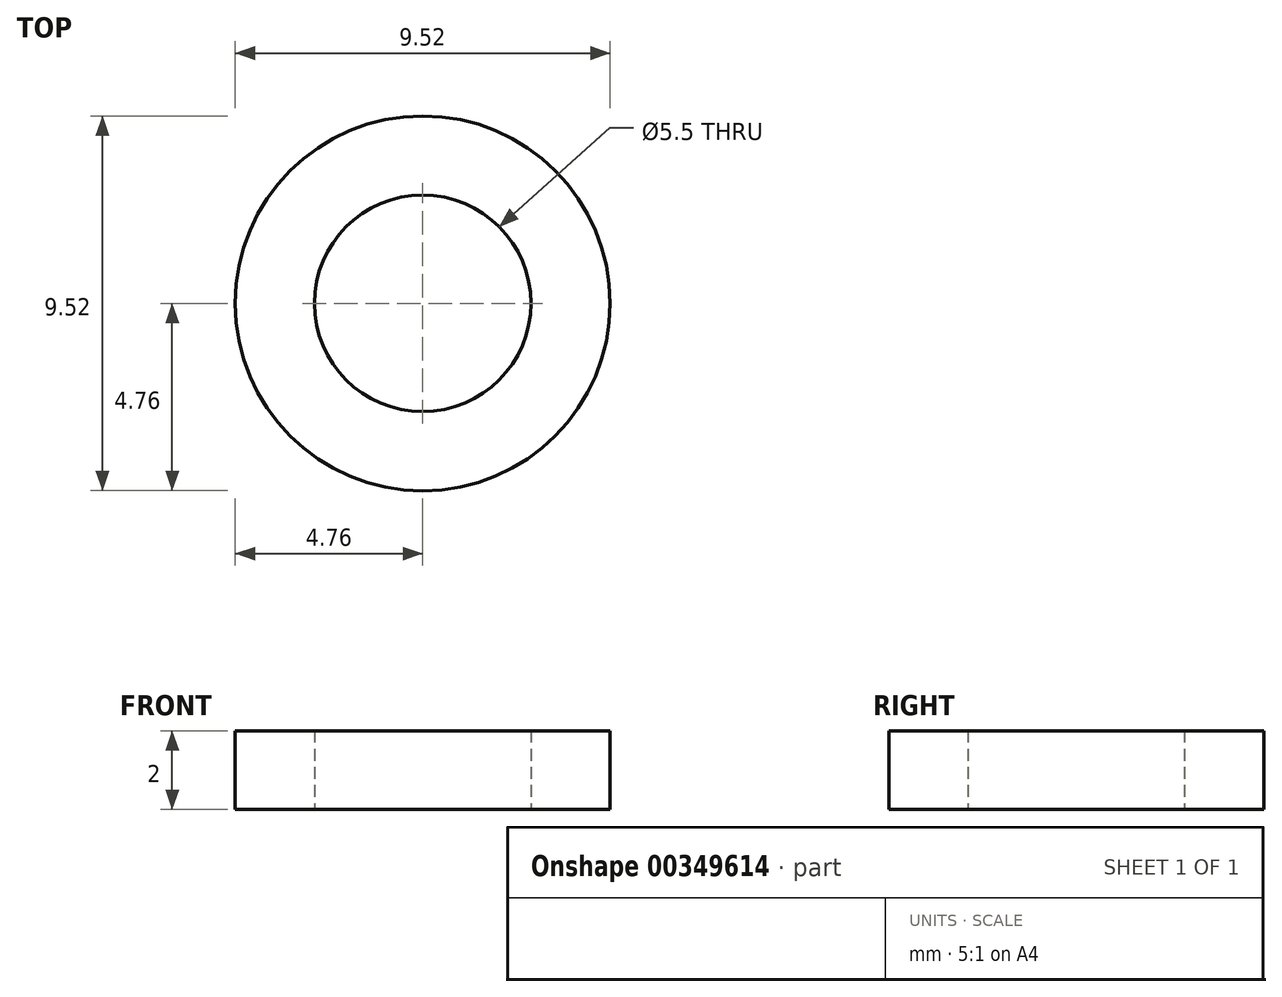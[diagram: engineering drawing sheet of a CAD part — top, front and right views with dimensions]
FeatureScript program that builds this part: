
annotation { "Feature Type Name" : "Feature", "Feature Type Description" : "" }
export const myFeature = defineFeature(function(context is Context, id is Id, definition is map)
    precondition{}
    {
        {
            var Q0;
            Q0=qCreatedBy(makeId("Top.planeOp"),FACE);
            var sketch = newSketch(context, id + "F0", { "sketchPlane" : qUnion([Q0])});
            skCircle(sketch, "E0", {"center": v(0, 0) * mm, "radius": 2.75 * mm});
            skCircle(sketch, "E1", {"center": v(0, 0) * mm, "radius": 4.76 * mm});
            skSolve(sketch);
        }
        {
            var Q0;
            Q0 = qSketchRegion(id + "F0", true);
            extrude(context, id + "F1", {"entities" : qUnion([Q0]), "depth" : 2 * mm});
        }
    });
